# Revit family: NLRS_57_DUA_UN_round_firedamper_fdcdd_LT_Solid_Air
name_source: partatom
category: Duct Accessories
units: mm (PartAtom-declared; Revit-internal decimal feet)

## family parameters
Always vertical = No
Cut with Voids When Loaded = No
Part Type = Breaks Into
Round Connector Dimension = Use Diameter
Shared = No
Work Plane-Based = No

## types (3) — shared parameters
Article_Data = FDCDD
Assembly Code = 57.70
Blade material = Hittebestendig dikte 25mm
Casing material = Gegalvaniseerd plaatstaal
Description = Ronde brandklep
FireRating = EI60 S (ve i <->o), DoP 717/2022
Fuse temperatuur (default) = 72 °C
IfcDescription = Ronde brandklep
IfcExportAs = IfcDamperType
IfcExportType = FIREDAMPER
LoadBearing = No
Manufacturer = Solid Air Climate Solutions
Model = Brandklep - Rond
NLRS_C_content_datum_uitgifte = 21-11-2022
NLRS_C_content_provider = Solid Air Climate Systems
NLRS_C_content_versie = Versie 3.20.00
NLRS_C_description = Ronde brandklep
SACS_Dummy = 1
Selection_Factors = Selection_Factors
Show Symbol = Yes
URL = https://solid-air.nl
zero-valued in all types: Default Elevation

## per-type parameters (varying)
| type | SACS_Index2 |
| FDCDD O M24S | 3 mm  [stored 0.00984252 ft] |
| FDCDD O M230S | 4 mm  [stored 0.0131234 ft] |
| FDCDD O M24S-ST | 5 mm  [stored 0.0164042 ft] |

note: [stored X ft] marks values corroborated as IEEE doubles in the binary element streams (Revit-internal decimal feet)

## geometry (parser evidence)
native form markers: Sweep x8
no freeform markers — native parametric forms only
